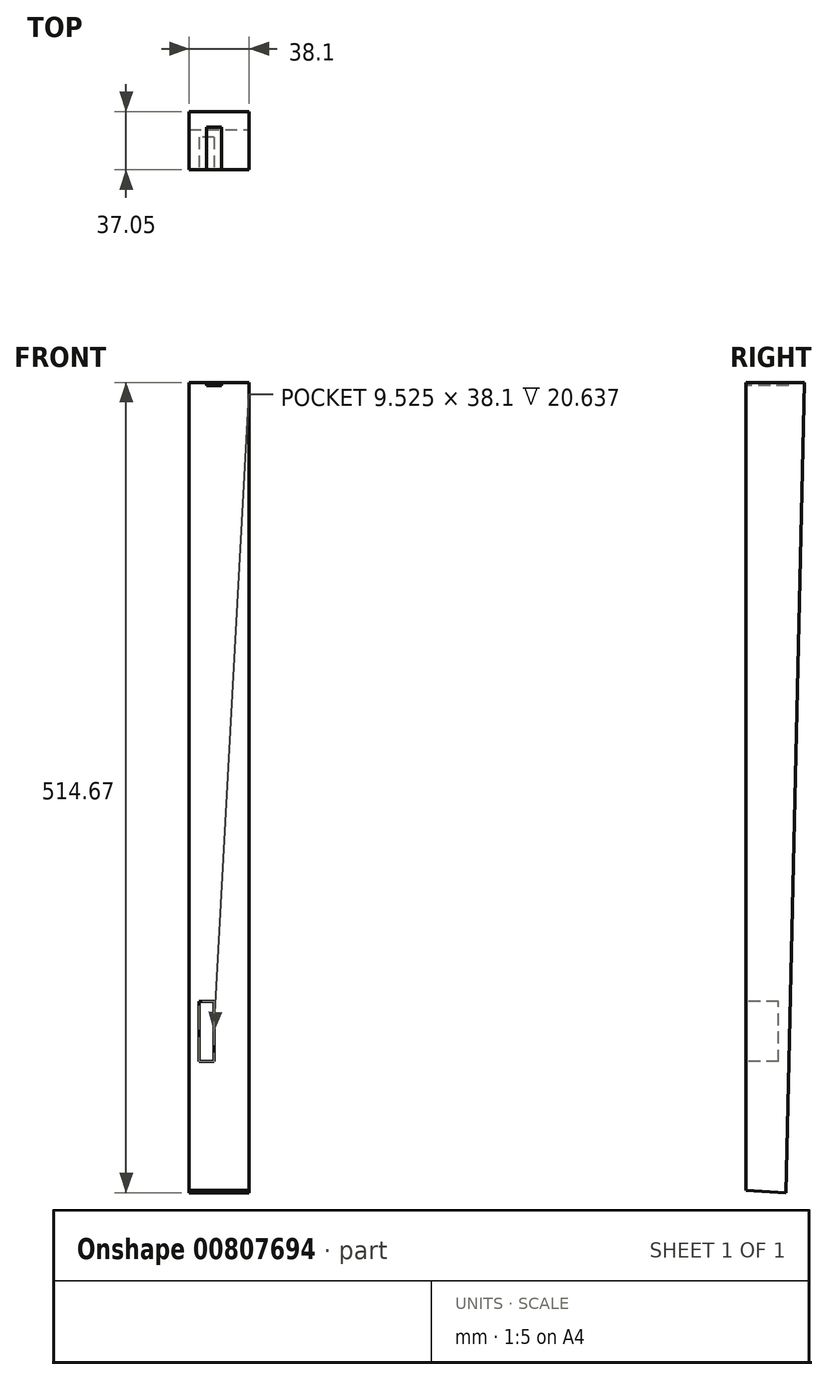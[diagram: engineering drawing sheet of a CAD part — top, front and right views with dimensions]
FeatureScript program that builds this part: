
annotation { "Feature Type Name" : "Feature", "Feature Type Description" : "" }
export const myFeature = defineFeature(function(context is Context, id is Id, definition is map)
    precondition{}
    {
        {
            var Q0;
            Q0=qCreatedBy(makeId("Top.planeOp"),FACE);
            var sketch = newSketch(context, id + "F0", { "sketchPlane" : qUnion([Q0])});
            skLineSegment(sketch, "E0.bottom", {"start": v(19.05, 19.05) * mm, "end": v(-19.05, 19.05) * mm});
            skLineSegment(sketch, "E0.top", {"start": v(19.05, -19.05) * mm, "end": v(-19.05, -19.05) * mm});
            skLineSegment(sketch, "E0.left", {"start": v(19.05, 19.05) * mm, "end": v(19.05, -19.05) * mm});
            skLineSegment(sketch, "E0.right", {"start": v(-19.05, 19.05) * mm, "end": v(-19.05, -19.05) * mm});
            skPoint(sketch, "E0.middle", {"position": v(0, 0) * mm});
            skSolve(sketch);
        }
        {
            var Q0;
            Q0=makeQuery(id+"F0.imprint","IMPRINT",FACE,{"disambiguationData":[TD([[makeQuery(id+"F0.imprint","IMPRINT",EDGE,{"derivedFrom":sQuery(id+"F0.wireOp",EDGE,"E0.bottom")}),1.0]])]});
            extrude(context, id + "F1", {"entities" : qUnion([Q0]), "oppositeDirection" : true, "depth" : 512.76 * mm, "hasSecondDirection" : true, "secondDirectionOppositeDirection" : false, "secondDirectionDepth" : ((22 + 3 / 32) - 20 - 3 / 16) * mm});
        }
        {
            var Q0;
            Q0=makeQuery(id+"F1.opExtrude","SWEPT_FACE",FACE,{"disambiguationData":[OSD([sQuery(id+"F0.wireOp",EDGE,"E0.top")])]});
            var sketch = newSketch(context, id + "F2", { "sketchPlane" : qUnion([Q0])});
            skLineSegment(sketch, "E1.bottom", {"start": v(-7.94, 0) * mm, "end": v(1.59, 0) * mm});
            skLineSegment(sketch, "E1.top", {"start": v(-7.94, 31.75) * mm, "end": v(1.59, 31.75) * mm});
            skLineSegment(sketch, "E1.left", {"start": v(-7.94, 0) * mm, "end": v(-7.94, 31.75) * mm});
            skLineSegment(sketch, "E1.right", {"start": v(1.59, 0) * mm, "end": v(1.59, 31.75) * mm});
            skLineSegment(sketch, "E2.bottom", {"start": v(-3.17, -429.42) * mm, "end": v(-12.7, -429.42) * mm});
            skLineSegment(sketch, "E2.top", {"start": v(-3.17, -391.32) * mm, "end": v(-12.7, -391.32) * mm});
            skLineSegment(sketch, "E2.left", {"start": v(-3.17, -429.42) * mm, "end": v(-3.17, -391.32) * mm});
            skLineSegment(sketch, "E2.right", {"start": v(-12.7, -429.42) * mm, "end": v(-12.7, -391.32) * mm});
            skSolve(sketch);
        }
        {
            var Q0;
            Q0=makeQuery(id+"F2.imprint","IMPRINT",FACE,{"disambiguationData":[TD([[makeQuery(id+"F2.imprint","IMPRINT",EDGE,{"derivedFrom":sQuery(id+"F2.wireOp",EDGE,"E2.bottom")}),-1.0]])]});
            extrude(context, id + "F3", {"entities" : qUnion([Q0]), "operationType" : NewBodyOperationType.REMOVE, "oppositeDirection" : true, "depth" : 20.64 * mm});
        }
        {
            var Q0;
            Q0=makeQuery(id+"F2.imprint","IMPRINT",FACE,{"disambiguationData":[TD([[makeQuery(id+"F2.imprint","IMPRINT",EDGE,{"derivedFrom":sQuery(id+"F2.wireOp",EDGE,"E1.bottom")}),1.0]])]});
            extrude(context, id + "F4", {"entities" : qUnion([Q0]), "operationType" : NewBodyOperationType.REMOVE, "oppositeDirection" : true, "depth" : 26.99 * mm});
        }
        {
            var Q0;
            Q0=makeQuery(id+"F2.imprint","IMPRINT",FACE,{"disambiguationData":[TD([[makeQuery(id+"F2.imprint","IMPRINT",EDGE,{"derivedFrom":sQuery(id+"F2.wireOp",EDGE,"E1.bottom")}),-1.0]])]});
            var sketch = newSketch(context, id + "F5", { "sketchPlane" : qUnion([Q0])});
            skLineSegment(sketch, "E3.0", {"start": v(19.05, -512.76) * mm, "end": v(19.05, 48.42) * mm});
            skLineSegment(sketch, "E4.0", {"start": v(19.05, -512.76) * mm, "end": v(0, -512.76) * mm});
            skLineSegment(sketch, "E5", {"start": v(0, -512.76) * mm, "end": v(19.05, 48.42) * mm});
            skPoint(sketch, "E6.orphan", {"position": v(-19.05, -512.76) * mm});
            skSolve(sketch);
        }
        {
            var Q0;
            Q0=makeQuery(id+"F5.imprint","IMPRINT",FACE,{"disambiguationData":[TD([[makeQuery(id+"F5.imprint","IMPRINT",EDGE,{"derivedFrom":sQuery(id+"F5.wireOp",EDGE,"E3.0")}),1.0]])]});
            extrude(context, id + "F6", {"entities" : qUnion([Q0]), "operationType" : NewBodyOperationType.REMOVE, "oppositeDirection" : true, "depth" : 38.1 * mm});
        }
        {
            var Q0;
            Q0=qCreatedBy(makeId("Right.planeOp"),FACE);
            var sketch = newSketch(context, id + "F7", { "sketchPlane" : qUnion([Q0])});
            skLineSegment(sketch, "E7.0", {"start": v(-19.05, 45.09) * mm, "end": v(-19.05, 48.42) * mm});
            skLineSegment(sketch, "E8", {"start": v(19.05, 48.42) * mm, "end": v(-19.05, 45.09) * mm});
            skLineSegment(sketch, "E9", {"start": v(-19.05, 48.42) * mm, "end": v(19.05, 48.42) * mm});
            skLineSegment(sketch, "E10.0", {"start": v(19.05, -512.76) * mm, "end": v(19.05, 48.42) * mm});
            skLineSegment(sketch, "E11", {"start": v(19.05, 48.42) * mm, "end": v(6.35, -512.76) * mm});
            skLineSegment(sketch, "E12", {"start": v(6.35, -512.76) * mm, "end": v(19.05, -512.76) * mm});
            skLineSegment(sketch, "E13.0", {"start": v(19.05, -512.76) * mm, "end": v(-19.05, -512.76) * mm});
            skLineSegment(sketch, "E14", {"start": v(6.35, -512.76) * mm, "end": v(-19.05, -511.43) * mm});
            skLineSegment(sketch, "E15", {"start": v(-19.05, -511.43) * mm, "end": v(-19.05, -512.76) * mm});
            skSolve(sketch);
        }
        {
            var Q0;
            {var subQ0=sQuery(id+"F7.wireOp",EDGE,"E10.0");Q0=makeQuery(id+"F7.imprint","IMPRINT",FACE,{"disambiguationData":[TD([[makeQuery(id+"F7.imprint","IMPRINT",EDGE,{"derivedFrom":subQ0}),1.0]])]});}
            var Q1;
            {var subQ0=sQuery(id+"F7.wireOp",EDGE,"E14");Q1=makeQuery(id+"F7.imprint","IMPRINT",FACE,{"disambiguationData":[TD([[makeQuery(id+"F7.imprint","IMPRINT",EDGE,{"derivedFrom":subQ0}),1.0]])]});}
            var Q2;
            Q2=makeQuery(id+"F7.imprint","IMPRINT",FACE,{"disambiguationData":[TD([[makeQuery(id+"F7.imprint","IMPRINT",EDGE,{"derivedFrom":sQuery(id+"F7.wireOp",EDGE,"E7.0")}),-1.0]])]});
            extrude(context, id + "F8", {"entities" : qUnion([Q0, Q1, Q2]), "operationType" : NewBodyOperationType.REMOVE, "endBound" : BoundingType.SYMMETRIC, "oppositeDirection" : true, "depth" : 38.1 * mm});
        }
    });
